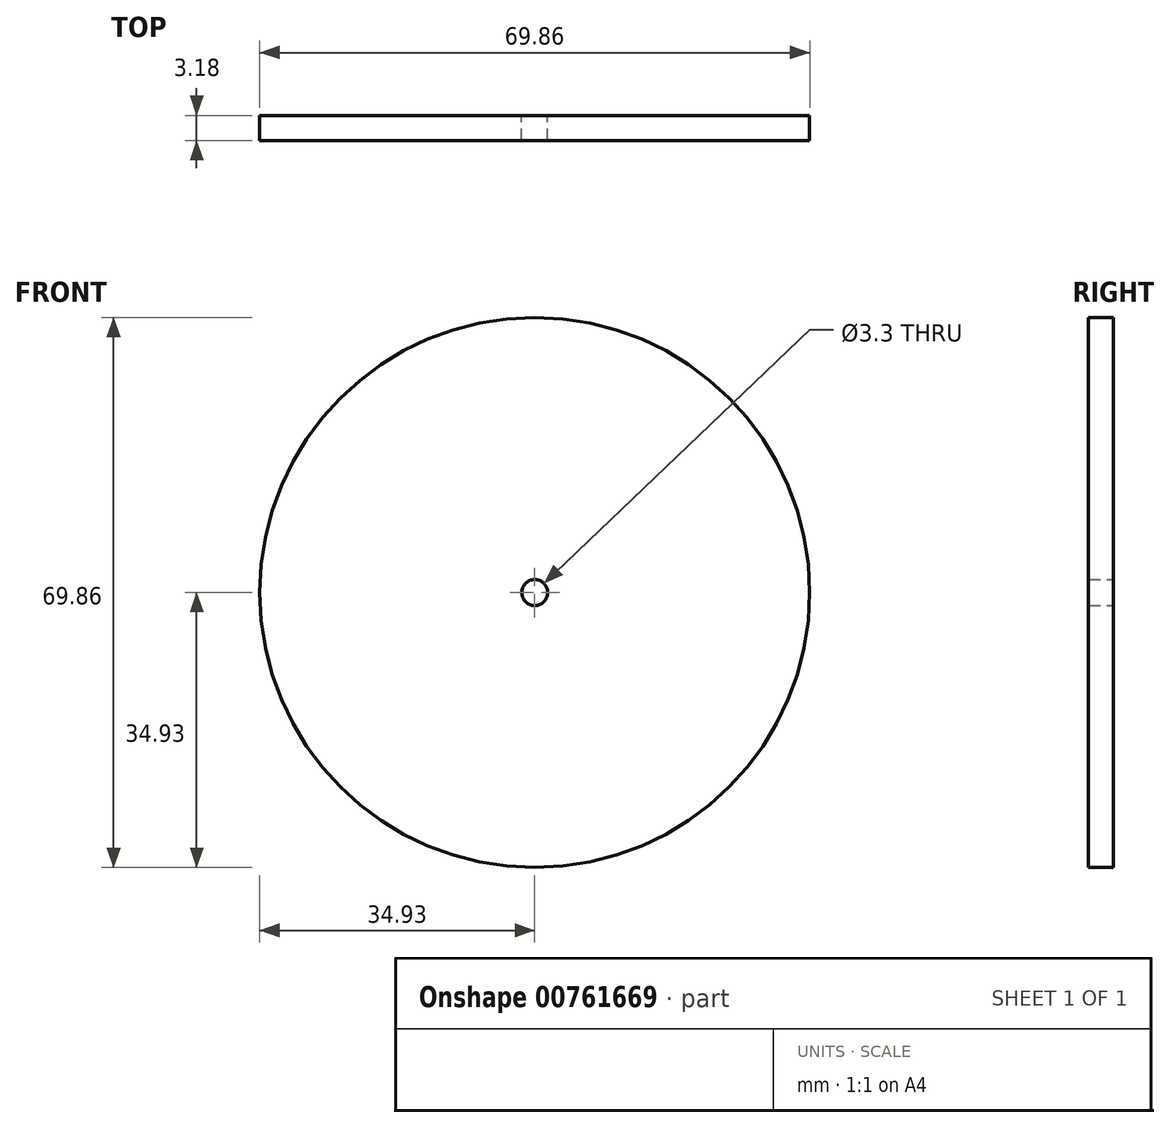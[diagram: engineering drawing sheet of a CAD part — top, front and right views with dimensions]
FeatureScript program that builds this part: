
annotation { "Feature Type Name" : "Feature", "Feature Type Description" : "" }
export const myFeature = defineFeature(function(context is Context, id is Id, definition is map)
    precondition{}
    {
        {
            var Q0;
            Q0=qCreatedBy(makeId("Front.planeOp"),FACE);
            var sketch = newSketch(context, id + "F0", { "sketchPlane" : qUnion([Q0])});
            skCircle(sketch, "E0", {"center": v(0, 0) * mm, "radius": 34.93 * mm});
            skCircle(sketch, "E1", {"center": v(0, 0) * mm, "radius": 1.65 * mm});
            skSolve(sketch);
        }
        {
            var Q0;
            Q0 = qSketchRegion(id + "F0", true);
            extrude(context, id + "F1", {"entities" : qUnion([Q0]), "depth" : 3.17 * mm, "offsetDistance" : 25.4 * mm});
        }
    });
